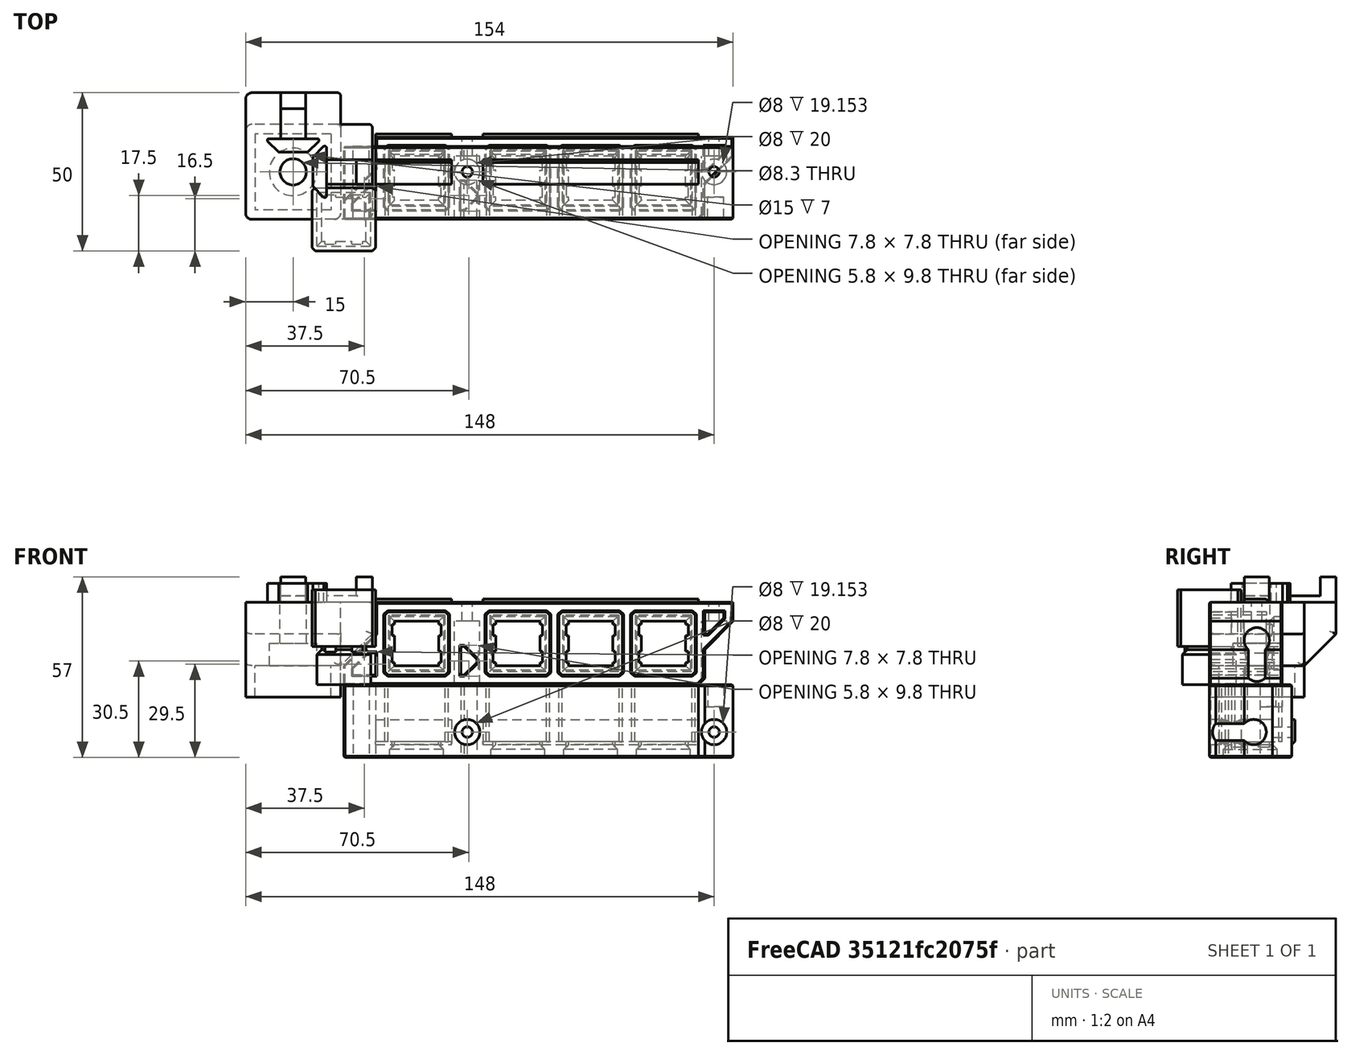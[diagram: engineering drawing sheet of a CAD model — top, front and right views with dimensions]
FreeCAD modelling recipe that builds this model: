
FCSTD DOCUMENT  (FreeCAD 0.19R24291 (Git))
Label: cherry-mx-button
License: Other
LicenseURL: GPL3
objects: Part::Box×17, Part::Chamfer×11, Part::MultiFuse×8, Part::Feature×7, Part::Cut×7, Part::Cylinder×2, Part::Refine×2
note: 54 computed .brp shape members not serialized (recipe doc carries the construction recipe); baked Part::Feature solids carry a one-line shape summary decoded from their .brp

FEATURE [Part::Feature] Cut008004003004014002002005  label="foot002"
  Placement = pos=(-16,15,-4) rot=(0,0,1;3.14159rad)
  shape: bbox 40.3 x 40.3 x 38.3 mm, 68 faces (baked)
FEATURE [Part::Box] Box  label="Cube"
  AttacherType = Attacher::AttachEngine3D
  Height = 16
  Length = 11
  Width = 30
FEATURE [Part::Box] Box001  label="Cube001"
  AttacherType = Attacher::AttachEngine3D
  Height = 26
  Length = 104
  Placement = pos=(10,0,0) rot=(0,0,1;0rad)
  Width = 30
FEATURE [Part::Chamfer] Chamfer
  Base = -> Box
  Edges = 1 edges r=10: [Edge2]
FEATURE [Part::Box] Box003  label="Cube003"
  AttacherType = Attacher::AttachEngine3D
  Height = 1
  Length = 14
  Placement = pos=(-7,-7,11) rot=(0,0,1;0rad)
  Width = 14
FEATURE [Part::Box] Box004  label="Cube004"
  AttacherType = Attacher::AttachEngine3D
  Height = 11
  Length = 17
  Placement = pos=(-8.5,-8.5,0) rot=(0,0,1;0rad)
  Width = 17
FEATURE [Part::Chamfer] Chamfer002
  Base = -> Box004
  Edges = 4 edges r=1.5: [Edge2,Edge6,Edge10,Edge12]
FEATURE [Part::Box] Box005  label="Cube005"
  AttacherType = Attacher::AttachEngine3D
  Height = 18
  Length = 20
  Placement = pos=(-10,-10,12) rot=(0,0,1;0rad)
  Width = 20
FEATURE [Part::Chamfer] Chamfer003
  Base = -> Box005
  Edges = 4 edges r=1: [Edge1,Edge3,Edge5,Edge7]
FEATURE [Part::Box] Box006  label="Cube006"
  AttacherType = Attacher::AttachEngine3D
  Height = 2
  Length = 3.5
  Placement = pos=(-6,-7.8,10) rot=(0,0,1;0rad)
  Width = 1
FEATURE [Part::Box] Box007  label="Cube007"
  AttacherType = Attacher::AttachEngine3D
  Height = 2
  Length = 3.5
  Placement = pos=(2.5,-7.8,10) rot=(0,0,1;0rad)
  Width = 1
FEATURE [Part::Box] Box008  label="Cube008"
  AttacherType = Attacher::AttachEngine3D
  Height = 2
  Length = 3.5
  Placement = pos=(2.5,6.8,10) rot=(0,0,1;0rad)
  Width = 1
FEATURE [Part::Box] Box009  label="Cube009"
  AttacherType = Attacher::AttachEngine3D
  Height = 2
  Length = 3.5
  Placement = pos=(-6,6.8,10) rot=(0,0,1;0rad)
  Width = 1
FEATURE [Part::MultiFuse] Fusion
  Shapes = -> [Box009,Box008,Box007,Box006]
FEATURE [Part::MultiFuse] Fusion001  label="button-slot"
  Shapes = -> [Fusion,Chamfer003,Chamfer002,Box003]
FEATURE [Part::Feature] Fusion001001  label="button-slot001"
  Placement = pos=(23,30,13) rot=(0.57735,-0.57735,0.57735;2.0944rad)
  shape: bbox 20 x 30 x 20 mm, 39 faces (baked)
FEATURE [Part::Cylinder] Cylinder
  Angle = 360
  AttacherType = Attacher::AttachEngine3D
  Height = 20
  Placement = pos=(43,15,0) rot=(0,0,1;0rad)
  Radius = 4
FEATURE [Part::Cylinder] Cylinder001
  Angle = 360
  AttacherType = Attacher::AttachEngine3D
  Height = 34
  Placement = pos=(43,15,0) rot=(0,0,1;0rad)
  Radius = 1.65
FEATURE [Part::MultiFuse] Fusion001002  label="m3-slot"
  Placement = pos=(-4,0,0) rot=(0,0,1;0rad)
  Shapes = -> [Cylinder001,Cylinder]
FEATURE [Part::Feature] Fusion001003  label="button-slot002"
  Placement = pos=(55,30,13) rot=(0.57735,-0.57735,0.57735;2.0944rad)
  shape: bbox 20 x 30 x 20 mm, 39 faces (baked)
FEATURE [Part::Feature] Fusion001004  label="button-slot003"
  Placement = pos=(78,30,13) rot=(0.57735,-0.57735,0.57735;2.0944rad)
  shape: bbox 20 x 30 x 20 mm, 39 faces (baked)
FEATURE [Part::Feature] Fusion001005  label="button-slot004"
  Placement = pos=(101,30,13) rot=(0.57735,-0.57735,0.57735;2.0944rad)
  shape: bbox 20 x 30 x 20 mm, 39 faces (baked)
FEATURE [Part::Feature] Fusion001002001  label="m3-slot001"
  Placement = pos=(74,0,0) rot=(0,0,1;0rad)
  shape: bbox 8 x 8 x 34 mm, 6 faces (baked)
FEATURE [Part::Box] Box010  label="Cube010"
  AttacherType = Attacher::AttachEngine3D
  Height = 15
  Length = 10
  Placement = pos=(119,0,11) rot=(0,0,1;0rad)
  Width = 30
FEATURE [Part::Chamfer] Chamfer007
  Base = -> Box010
  Edges = 1 edges r=9: [Edge8]
  Placement = pos=(-6,0,0) rot=(0,0,1;0rad)
FEATURE [Part::MultiFuse] Fusion001002002
  Shapes = -> [Chamfer,Box001,Chamfer007]
FEATURE [Part::MultiFuse] Fusion001002003
  Shapes = -> [Fusion001005,Fusion001004,Fusion001003,Fusion001001]
FEATURE [Part::Cut] Cut
  Base = -> Fusion001002002
  Tool = -> Fusion001002003
FEATURE [Part::MultiFuse] Fusion001002004
  Shapes = -> [Fusion001002,Fusion001002001]
FEATURE [Part::Chamfer] Chamfer008
  Base = -> Cut
  Edges = 1 edges r=2: [Edge59]
FEATURE [Part::Box] Box011  label="Cube011"
  AttacherType = Attacher::AttachEngine3D
  Height = 7
  Length = 7
  Placement = pos=(3,0,3) rot=(0,0,1;0rad)
  Width = 30
FEATURE [Part::Chamfer] Chamfer011
  Base = -> Box011
  Edges = 1 edges r=5: [Edge2]
FEATURE [Part::Cut] Cut008004003004014002002006
  Base = -> Chamfer008
  Tool = -> Chamfer011
FEATURE [Part::Box] Box012  label="Cube012"
  AttacherType = Attacher::AttachEngine3D
  Height = 2
  Length = 113
  Placement = pos=(10,11.1,25) rot=(0,0,1;0rad)
  Width = 7.8
FEATURE [Part::Chamfer] Chamfer012
  Base = -> Box012
  Edges = 1 edges r=1: [Edge12]
FEATURE [Part::MultiFuse] Fusion001002005
  Shapes = -> [Box012,Chamfer012,Cut008004003004014002002006]
FEATURE [Part::Box] Box015  label="Cube015"
  AttacherType = Attacher::AttachEngine3D
  Height = 9
  Length = 5
  Placement = pos=(36,0,11) rot=(0,0,1;0rad)
  Width = 30
FEATURE [Part::Chamfer] Chamfer013
  Base = -> Box015
  Edges = 2 edges r=4: [Edge6,Edge8]
  Placement = pos=(1,0,-8) rot=(0,0,1;0rad)
FEATURE [Part::Cut] Cut008004003004014002002007
  Base = -> Fusion001002005
  Tool = -> Chamfer013
FEATURE [Part::Cut] Cut008004003004014002002008
  Base = -> Cut008004003004014002002007
  Tool = -> Fusion001002004
FEATURE [Part::Refine] Cut008004003004014002002008001
  Source = -> Cut008004003004014002002008
FEATURE [Part::Box] Box016  label="Cube016"
  AttacherType = Attacher::AttachEngine3D
  Height = 26
  Length = 124
  Placement = pos=(0,23,0) rot=(0,0,1;0rad)
  Width = 10
FEATURE [Part::Cut] Cut008004003004014002002008002
  Base = -> Cut008004003004014002002008001
  Tool = -> Box016
FEATURE [Part::Box] Box017  label="Cube017"
  AttacherType = Attacher::AttachEngine3D
  Height = 7
  Length = 6
  Placement = pos=(114,0,16) rot=(0,0,1;0rad)
  Width = 10
FEATURE [Part::Chamfer] Chamfer014
  Base = -> Box017
  Edges = 1 edges r=5: [Edge8]
  Placement = pos=(0,-3,0) rot=(0,0,1;0rad)
FEATURE [Part::Cut] Cut008004003004014002002008003
  Base = -> Cut008004003004014002002008002
  Tool = -> Chamfer014
FEATURE [Part::Chamfer] Chamfer015
  Base = -> Cut008004003004014002002008003
  Edges = 94 edges r=0.4: [Edge1,Edge5,Edge7,Edge8,Edge9,Edge10,Edge11,Edge12,Edge13,Edge14,Edge15,Edge16,Edge17,Edge18,Edge19,Edge20,Edge21,Edge22,Edge23,Edge24,Edge25,Edge26,Edge27,Edge28,Edge29,Edge30,Edge31,Edge32,Edge33,Edge34,Edge35,Edge36,Edge37,Edge38,Edge39,Edge40,Edge41,Edge42,Edge43,Edge44,Edge45,Edge46,Edge47,+51 more]
FEATURE [Part::Chamfer] Chamfer016
  Base = -> Chamfer015
  Edges = 1 edges r=0.99: [Edge338]
FEATURE [Part::Box] Box018  label="Cube018"
  AttacherType = Attacher::AttachEngine3D
  Height = 10
  Length = 10
  Placement = pos=(34,10,26) rot=(0,0,1;0rad)
  Width = 10
FEATURE [Part::Box] Box019  label="Cube019"
  AttacherType = Attacher::AttachEngine3D
  Height = 10
  Length = 11
  Placement = pos=(112,10,26) rot=(0,0,1;0rad)
  Width = 10
FEATURE [Part::MultiFuse] Fusion001002006
  Shapes = -> [Box019,Box018]
FEATURE [Part::Cut] Cut008004003004014002002008004
  Base = -> Chamfer016
  Tool = -> Fusion001002006
FEATURE [Part::Refine] Cut008004003004014002002008004001
  Source = -> Cut008004003004014002002008004
FEATURE [Part::Feature] Cut008004003004014002002008004001001
  Placement = pos=(0,0,0) rot=(1,0,0;4.71239rad)
  shape: bbox 123 x 27 x 23 mm, 296 faces (baked)
